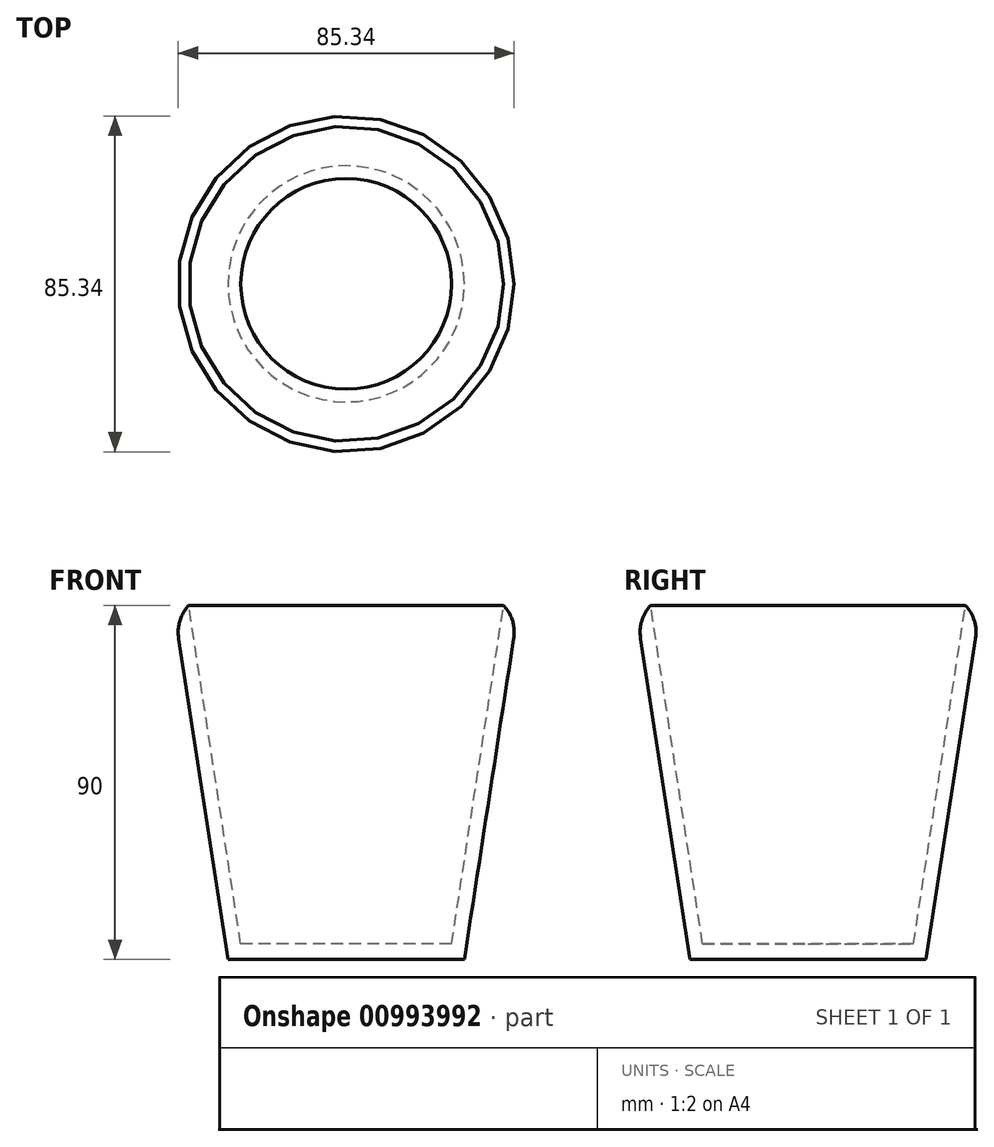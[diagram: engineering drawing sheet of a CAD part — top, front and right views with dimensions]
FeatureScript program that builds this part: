
annotation { "Feature Type Name" : "Feature", "Feature Type Description" : "" }
export const myFeature = defineFeature(function(context is Context, id is Id, definition is map)
    precondition{}
    {
        {
            var Q0;
            Q0=qCreatedBy(makeId("Front.planeOp"),FACE);
            var sketch = newSketch(context, id + "F0", { "sketchPlane" : qUnion([Q0])});
            skLineSegment(sketch, "E0", {"start": v(0, 0) * mm, "end": v(-30, 0) * mm});
            skLineSegment(sketch, "E1", {"start": v(-30, 0) * mm, "end": v(-43.84, 90) * mm});
            skLineSegment(sketch, "E2", {"start": v(-43.84, 90) * mm, "end": v(-40, 90) * mm});
            skLineSegment(sketch, "E3", {"start": v(-40, 90) * mm, "end": v(-26.77, 4) * mm});
            skLineSegment(sketch, "E4", {"start": v(-26.77, 4) * mm, "end": v(0, 4) * mm});
            skLineSegment(sketch, "E5", {"start": v(0, 4) * mm, "end": v(0, 0) * mm});
            skSolve(sketch);
        }
        {
            var Q0;
            Q0=makeQuery(id+"F0.imprint","IMPRINT",FACE,{"disambiguationData":[TD([[makeQuery(id+"F0.imprint","IMPRINT",EDGE,{"derivedFrom":sQuery(id+"F0.wireOp",EDGE,"E0")}),-1.0]])]});
            var Q1;
            Q1=sQuery(id+"F0.wireOp",EDGE,"E5");
            revolve(context, id + "F1", {"surfaceOperationType" : NewSurfaceOperationType.NEW, "entities" : qUnion([Q0]), "axis" : qUnion([Q1]), "revolveType" : RevolveType.ONE_DIRECTION, "angle" : 360 * degree});
        }
        {
            var Q0;
            Q0=makeQuery(id+"F1.opRevolve","SWEPT_EDGE",EDGE,{"disambiguationData":[OSD([sQuery(id+"F0.wireOp",EDGE,"E1"),sQuery(id+"F0.wireOp",EDGE,"E2")])]});
            fillet(context, id + "F2", {"entities" : qUnion([Q0]), "radius" : 10.45 * mm, "tangentPropagation" : true, "rho" : 0.5, "crossSection" : FilletCrossSection.CONIC, "allowEdgeOverflow" : false});
        }
    });
